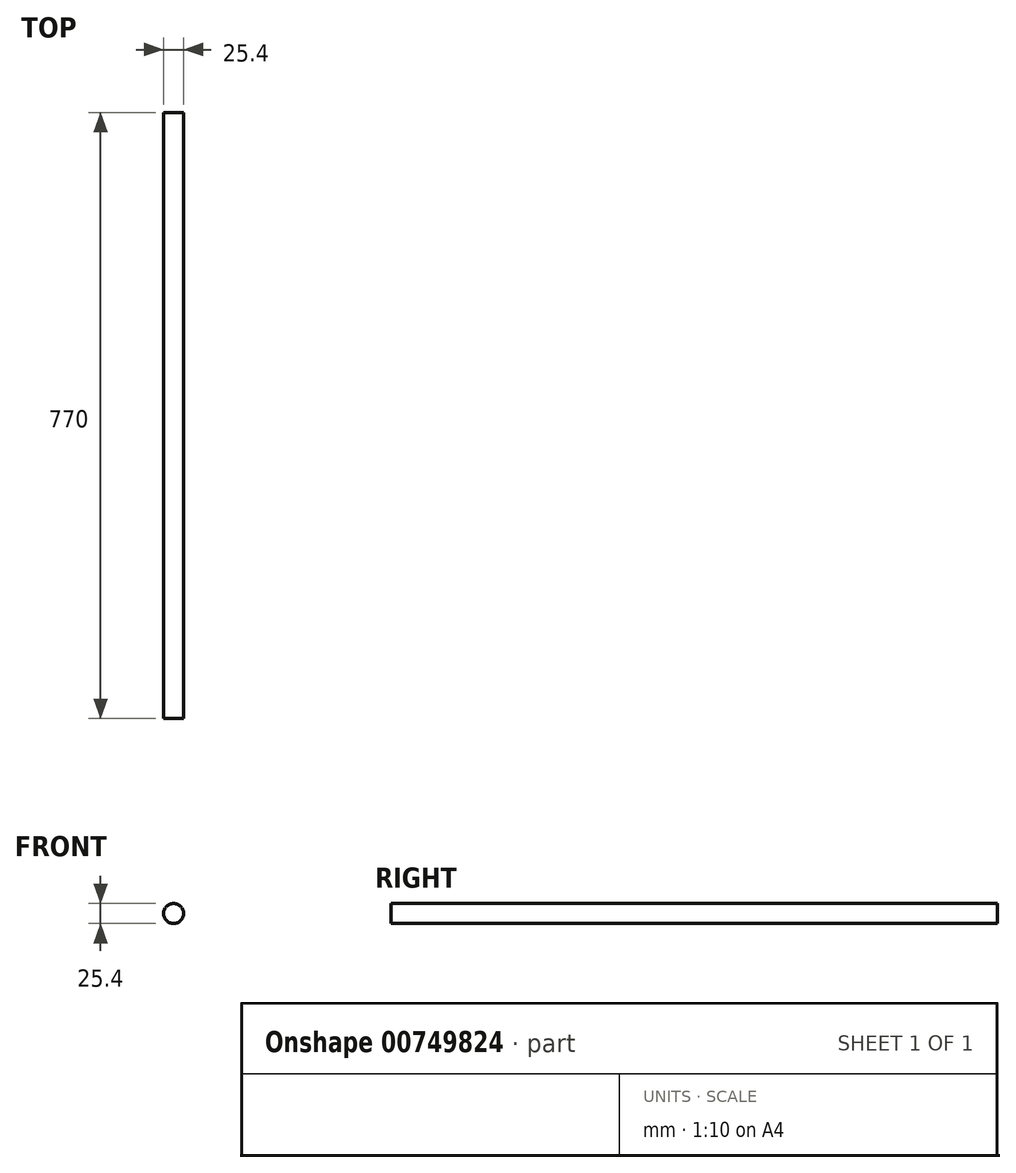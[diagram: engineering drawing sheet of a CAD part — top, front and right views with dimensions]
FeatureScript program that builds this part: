
annotation { "Feature Type Name" : "Feature", "Feature Type Description" : "" }
export const myFeature = defineFeature(function(context is Context, id is Id, definition is map)
    precondition{}
    {
        {
            var Q0;
            Q0=qCreatedBy(makeId("Front.planeOp"),FACE);
            var sketch = newSketch(context, id + "F0", { "sketchPlane" : qUnion([Q0])});
            skCircle(sketch, "E0", {"center": v(0, 0) * mm, "radius": 12.7 * mm});
            skSolve(sketch);
        }
        {
            var Q0;
            Q0=sQuery(id+"F0.wireOp",EDGE,"E0");
            extrude(context, id + "F1", {"bodyType" : ToolBodyType.SURFACE, "surfaceEntities" : qUnion([Q0]), "depth" : 770 * mm, "offsetDistance" : 25.4 * mm});
        }
    });
